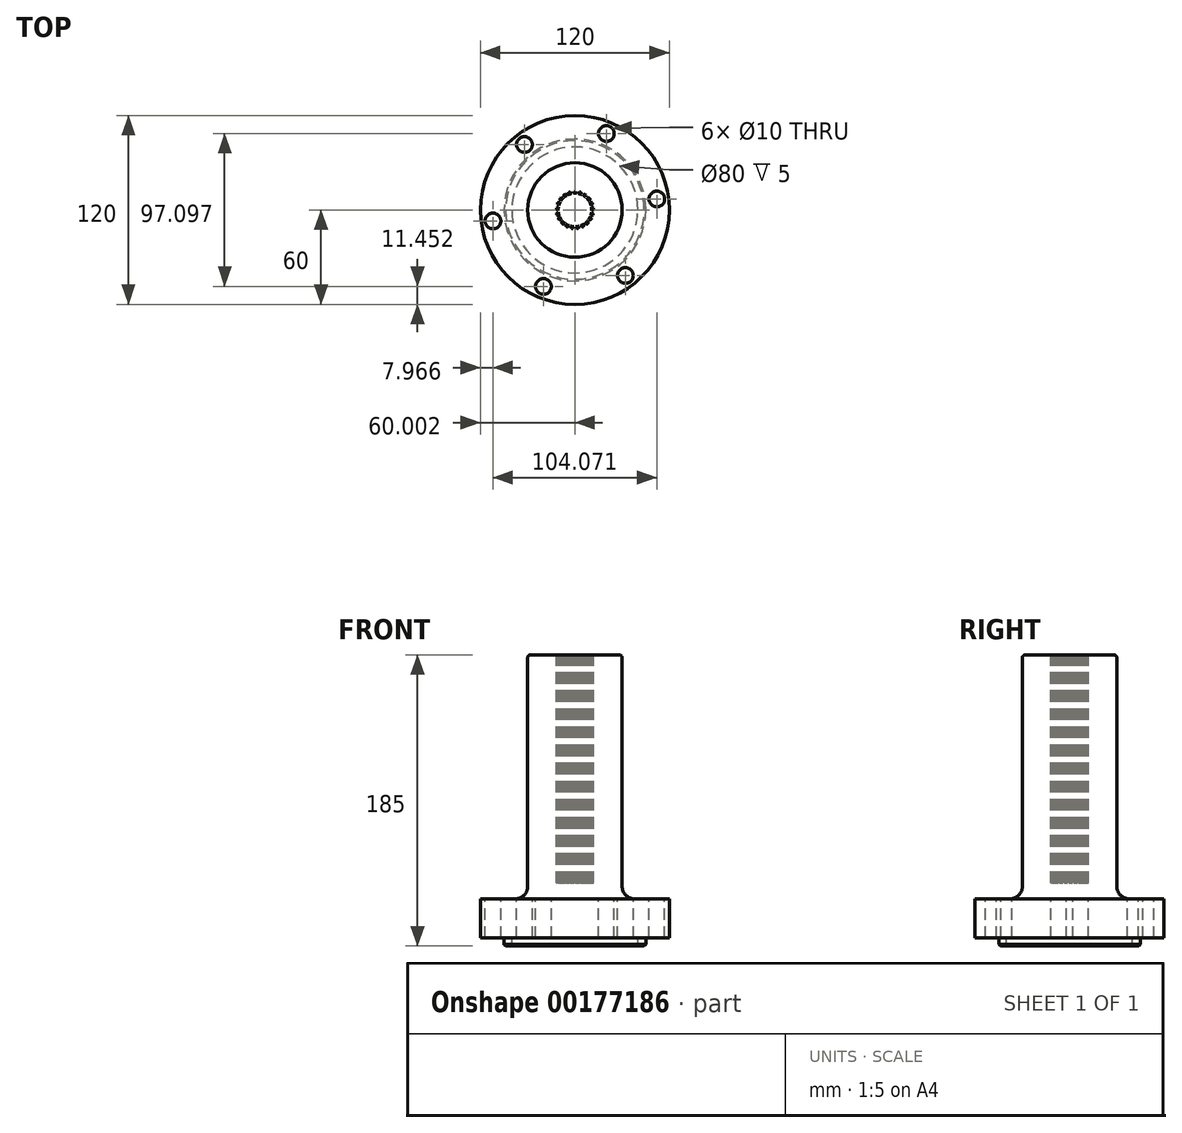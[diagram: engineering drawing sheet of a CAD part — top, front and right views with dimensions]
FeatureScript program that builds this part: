
annotation { "Feature Type Name" : "Feature", "Feature Type Description" : "" }
export const myFeature = defineFeature(function(context is Context, id is Id, definition is map)
    precondition{}
    {
        {
            var Q0;
            Q0=qCreatedBy(makeId("Front.planeOp"),FACE);
            var sketch = newSketch(context, id + "F0", { "sketchPlane" : qUnion([Q0])});
            skLineSegment(sketch, "E0", {"start": v(259.02, -43.78) * mm, "end": v(259.02, -223.78) * mm});
            skLineSegment(sketch, "E1", {"start": v(259.02, -223.78) * mm, "end": v(319.02, -223.78) * mm});
            skLineSegment(sketch, "E2", {"start": v(319.02, -223.78) * mm, "end": v(319.02, -198.78) * mm});
            skLineSegment(sketch, "E3", {"start": v(319.02, -198.78) * mm, "end": v(289.02, -198.78) * mm});
            skLineSegment(sketch, "E4", {"start": v(289.02, -198.78) * mm, "end": v(289.02, -43.78) * mm});
            skLineSegment(sketch, "E5", {"start": v(289.02, -43.78) * mm, "end": v(259.02, -43.78) * mm});
            skSolve(sketch);
        }
        {
            var Q0;
            Q0 = qSketchRegion(id + "F0", true);
            var Q1;
            Q1=sQuery(id+"F0.wireOp",EDGE,"E0");
            revolve(context, id + "F1", {"surfaceOperationType" : NewSurfaceOperationType.NEW, "entities" : qUnion([Q0]), "axis" : qUnion([Q1]), "revolveType" : RevolveType.FULL});
        }
        {
            var Q0;
            Q0=makeQuery(id+"F1.opRevolve","SWEPT_FACE",FACE,{"disambiguationData":[OSD([sQuery(id+"F0.wireOp",EDGE,"E5")])]});
            var sketch = newSketch(context, id + "F2", { "sketchPlane" : qUnion([Q0])});
            skCircle(sketch, "E6", {"center": v(259.02, 0) * mm, "radius": 11.83 * mm});
            skCircle(sketch, "E7", {"center": v(259.02, 0) * mm, "radius": 10.62 * mm});
            skLineSegment(sketch, "E8", {"start": v(258.54, -10.6) * mm, "end": v(257.73, -11.76) * mm});
            skLineSegment(sketch, "E9", {"start": v(259.5, -10.6) * mm, "end": v(260.3, -11.76) * mm});
            skLineSegment(sketch, "E10", {"start": v(258.54, -10.6) * mm, "end": v(259.5, -10.6) * mm});
            skLineSegment(sketch, "E11", {"start": v(257.73, -11.76) * mm, "end": v(260.3, -11.76) * mm});
            skPoint(sketch, "E12", {"position": v(259.02, -10.6) * mm});
            skPoint(sketch, "E13", {"position": v(259.02, -11.76) * mm});
            skLineSegment(sketch, "E14.1.0", {"start": v(261.7, -10.28) * mm, "end": v(262.6, -10) * mm});
            skLineSegment(sketch, "E14.1.1", {"start": v(262.6, -10) * mm, "end": v(263.72, -10.86) * mm});
            skLineSegment(sketch, "E14.1.2", {"start": v(261.7, -10.28) * mm, "end": v(261.26, -11.62) * mm});
            skLineSegment(sketch, "E14.1.3", {"start": v(261.26, -11.62) * mm, "end": v(263.72, -10.86) * mm});
            skLineSegment(sketch, "E14.2.0", {"start": v(264.6, -9.04) * mm, "end": v(265.4, -8.5) * mm});
            skLineSegment(sketch, "E14.2.1", {"start": v(265.4, -8.5) * mm, "end": v(266.7, -9) * mm});
            skLineSegment(sketch, "E14.2.2", {"start": v(264.6, -9.04) * mm, "end": v(264.58, -10.44) * mm});
            skLineSegment(sketch, "E14.2.3", {"start": v(264.58, -10.44) * mm, "end": v(266.7, -9) * mm});
            skLineSegment(sketch, "E14.3.0", {"start": v(267.02, -6.99) * mm, "end": v(267.62, -6.24) * mm});
            skLineSegment(sketch, "E14.3.1", {"start": v(267.62, -6.24) * mm, "end": v(269.02, -6.33) * mm});
            skLineSegment(sketch, "E14.3.2", {"start": v(267.02, -6.99) * mm, "end": v(267.41, -8.34) * mm});
            skLineSegment(sketch, "E14.3.3", {"start": v(267.41, -8.34) * mm, "end": v(269.02, -6.33) * mm});
            skLineSegment(sketch, "E14.4.0", {"start": v(268.72, -4.32) * mm, "end": v(269.07, -3.43) * mm});
            skLineSegment(sketch, "E14.4.1", {"start": v(269.07, -3.43) * mm, "end": v(270.44, -3.1) * mm});
            skLineSegment(sketch, "E14.4.2", {"start": v(268.72, -4.32) * mm, "end": v(269.5, -5.5) * mm});
            skLineSegment(sketch, "E14.4.3", {"start": v(269.5, -5.5) * mm, "end": v(270.44, -3.1) * mm});
            skLineSegment(sketch, "E14.5.0", {"start": v(269.57, -1.27) * mm, "end": v(269.64, -0.31) * mm});
            skLineSegment(sketch, "E14.5.1", {"start": v(269.64, -0.31) * mm, "end": v(270.85, 0.4) * mm});
            skLineSegment(sketch, "E14.5.2", {"start": v(269.57, -1.27) * mm, "end": v(270.65, -2.16) * mm});
            skLineSegment(sketch, "E14.5.3", {"start": v(270.65, -2.16) * mm, "end": v(270.85, 0.4) * mm});
            skLineSegment(sketch, "E14.6.0", {"start": v(269.47, 1.9) * mm, "end": v(269.26, 2.83) * mm});
            skLineSegment(sketch, "E14.6.1", {"start": v(269.26, 2.83) * mm, "end": v(270.2, 3.87) * mm});
            skLineSegment(sketch, "E14.6.2", {"start": v(269.47, 1.9) * mm, "end": v(270.77, 1.36) * mm});
            skLineSegment(sketch, "E14.6.3", {"start": v(270.77, 1.36) * mm, "end": v(270.2, 3.87) * mm});
            skLineSegment(sketch, "E14.7.0", {"start": v(268.45, 4.89) * mm, "end": v(267.97, 5.72) * mm});
            skLineSegment(sketch, "E14.7.1", {"start": v(267.97, 5.72) * mm, "end": v(268.56, 7) * mm});
            skLineSegment(sketch, "E14.7.2", {"start": v(268.45, 4.89) * mm, "end": v(269.85, 4.77) * mm});
            skLineSegment(sketch, "E14.7.3", {"start": v(269.85, 4.77) * mm, "end": v(268.56, 7) * mm});
            skLineSegment(sketch, "E14.8.0", {"start": v(266.59, 7.45) * mm, "end": v(265.89, 8.1) * mm});
            skLineSegment(sketch, "E14.8.1", {"start": v(265.89, 8.1) * mm, "end": v(266.08, 9.5) * mm});
            skLineSegment(sketch, "E14.8.2", {"start": v(266.59, 7.45) * mm, "end": v(267.96, 7.75) * mm});
            skLineSegment(sketch, "E14.8.3", {"start": v(267.96, 7.75) * mm, "end": v(266.08, 9.5) * mm});
            skLineSegment(sketch, "E14.9.0", {"start": v(264.06, 9.35) * mm, "end": v(263.2, 9.77) * mm});
            skLineSegment(sketch, "E14.9.1", {"start": v(263.2, 9.77) * mm, "end": v(262.96, 11.15) * mm});
            skLineSegment(sketch, "E14.9.2", {"start": v(264.06, 9.35) * mm, "end": v(265.28, 10.04) * mm});
            skLineSegment(sketch, "E14.9.3", {"start": v(265.28, 10.04) * mm, "end": v(262.96, 11.15) * mm});
            skLineSegment(sketch, "E14.10.0", {"start": v(261.08, 10.42) * mm, "end": v(260.13, 10.56) * mm});
            skLineSegment(sketch, "E14.10.1", {"start": v(260.13, 10.56) * mm, "end": v(259.5, 11.82) * mm});
            skLineSegment(sketch, "E14.10.2", {"start": v(261.08, 10.42) * mm, "end": v(262.05, 11.44) * mm});
            skLineSegment(sketch, "E14.10.3", {"start": v(262.05, 11.44) * mm, "end": v(259.5, 11.82) * mm});
            skLineSegment(sketch, "E14.11.0", {"start": v(257.92, 10.56) * mm, "end": v(256.97, 10.42) * mm});
            skLineSegment(sketch, "E14.11.1", {"start": v(256.97, 10.42) * mm, "end": v(256, 11.44) * mm});
            skLineSegment(sketch, "E14.11.2", {"start": v(257.92, 10.56) * mm, "end": v(258.54, 11.82) * mm});
            skLineSegment(sketch, "E14.11.3", {"start": v(258.54, 11.82) * mm, "end": v(256, 11.44) * mm});
            skLineSegment(sketch, "E14.12.0", {"start": v(254.85, 9.77) * mm, "end": v(253.99, 9.35) * mm});
            skLineSegment(sketch, "E14.12.1", {"start": v(253.99, 9.35) * mm, "end": v(252.76, 10.04) * mm});
            skLineSegment(sketch, "E14.12.2", {"start": v(254.85, 9.77) * mm, "end": v(255.08, 11.15) * mm});
            skLineSegment(sketch, "E14.12.3", {"start": v(255.08, 11.15) * mm, "end": v(252.76, 10.04) * mm});
            skLineSegment(sketch, "E14.13.0", {"start": v(252.16, 8.1) * mm, "end": v(251.45, 7.45) * mm});
            skLineSegment(sketch, "E14.13.1", {"start": v(251.45, 7.45) * mm, "end": v(250.08, 7.75) * mm});
            skLineSegment(sketch, "E14.13.2", {"start": v(252.16, 8.1) * mm, "end": v(251.97, 9.5) * mm});
            skLineSegment(sketch, "E14.13.3", {"start": v(251.97, 9.5) * mm, "end": v(250.08, 7.75) * mm});
            skLineSegment(sketch, "E14.14.0", {"start": v(250.07, 5.72) * mm, "end": v(249.6, 4.89) * mm});
            skLineSegment(sketch, "E14.14.1", {"start": v(249.6, 4.89) * mm, "end": v(248.2, 4.77) * mm});
            skLineSegment(sketch, "E14.14.2", {"start": v(250.07, 5.72) * mm, "end": v(249.48, 7) * mm});
            skLineSegment(sketch, "E14.14.3", {"start": v(249.48, 7) * mm, "end": v(248.2, 4.77) * mm});
            skLineSegment(sketch, "E14.15.0", {"start": v(248.79, 2.83) * mm, "end": v(248.57, 1.9) * mm});
            skLineSegment(sketch, "E14.15.1", {"start": v(248.57, 1.9) * mm, "end": v(247.27, 1.36) * mm});
            skLineSegment(sketch, "E14.15.2", {"start": v(248.79, 2.83) * mm, "end": v(247.84, 3.87) * mm});
            skLineSegment(sketch, "E14.15.3", {"start": v(247.84, 3.87) * mm, "end": v(247.27, 1.36) * mm});
            skLineSegment(sketch, "E14.16.0", {"start": v(248.4, -0.31) * mm, "end": v(248.48, -1.27) * mm});
            skLineSegment(sketch, "E14.16.1", {"start": v(248.48, -1.27) * mm, "end": v(247.4, -2.16) * mm});
            skLineSegment(sketch, "E14.16.2", {"start": v(248.4, -0.31) * mm, "end": v(247.2, 0.4) * mm});
            skLineSegment(sketch, "E14.16.3", {"start": v(247.2, 0.4) * mm, "end": v(247.4, -2.16) * mm});
            skLineSegment(sketch, "E14.17.0", {"start": v(248.97, -3.43) * mm, "end": v(249.32, -4.32) * mm});
            skLineSegment(sketch, "E14.17.1", {"start": v(249.32, -4.32) * mm, "end": v(248.55, -5.5) * mm});
            skLineSegment(sketch, "E14.17.2", {"start": v(248.97, -3.43) * mm, "end": v(247.6, -3.1) * mm});
            skLineSegment(sketch, "E14.17.3", {"start": v(247.6, -3.1) * mm, "end": v(248.55, -5.5) * mm});
            skLineSegment(sketch, "E14.18.0", {"start": v(250.43, -6.24) * mm, "end": v(251.03, -6.99) * mm});
            skLineSegment(sketch, "E14.18.1", {"start": v(251.03, -6.99) * mm, "end": v(250.63, -8.34) * mm});
            skLineSegment(sketch, "E14.18.2", {"start": v(250.43, -6.24) * mm, "end": v(249.03, -6.33) * mm});
            skLineSegment(sketch, "E14.18.3", {"start": v(249.03, -6.33) * mm, "end": v(250.63, -8.34) * mm});
            skLineSegment(sketch, "E14.19.0", {"start": v(252.65, -8.5) * mm, "end": v(253.44, -9.04) * mm});
            skLineSegment(sketch, "E14.19.1", {"start": v(253.44, -9.04) * mm, "end": v(253.46, -10.44) * mm});
            skLineSegment(sketch, "E14.19.2", {"start": v(252.65, -8.5) * mm, "end": v(251.33, -9) * mm});
            skLineSegment(sketch, "E14.19.3", {"start": v(251.33, -9) * mm, "end": v(253.46, -10.44) * mm});
            skLineSegment(sketch, "E14.20.0", {"start": v(255.44, -10) * mm, "end": v(256.35, -10.28) * mm});
            skLineSegment(sketch, "E14.20.1", {"start": v(256.35, -10.28) * mm, "end": v(256.79, -11.62) * mm});
            skLineSegment(sketch, "E14.20.2", {"start": v(255.44, -10) * mm, "end": v(254.33, -10.86) * mm});
            skLineSegment(sketch, "E14.20.3", {"start": v(254.33, -10.86) * mm, "end": v(256.79, -11.62) * mm});
            skSolve(sketch);
        }
        {
            var Q0;
            {var subQ0=sQuery(id+"F2.wireOp",EDGE,"E14.8.1");Q0=makeQuery(id+"F2.imprint","IMPRINT",FACE,{"disambiguationData":[TD([[makeQuery(id+"F2.imprint","IMPRINT",EDGE,{"derivedFrom":subQ0}),1.0]])]});}
            var Q1;
            {var subQ0=sQuery(id+"F2.wireOp",EDGE,"E10");Q1=makeQuery(id+"F2.imprint","IMPRINT",FACE,{"disambiguationData":[TD([[makeQuery(id+"F2.imprint","IMPRINT",EDGE,{"derivedFrom":subQ0}),1.0]])]});}
            var Q2;
            {var subQ0=sQuery(id+"F2.wireOp",EDGE,"E14.9.1");Q2=makeQuery(id+"F2.imprint","IMPRINT",FACE,{"disambiguationData":[TD([[makeQuery(id+"F2.imprint","IMPRINT",EDGE,{"derivedFrom":subQ0}),1.0]])]});}
            var Q3;
            {var subQ0=sQuery(id+"F2.wireOp",EDGE,"E14.10.1");Q3=makeQuery(id+"F2.imprint","IMPRINT",FACE,{"disambiguationData":[TD([[makeQuery(id+"F2.imprint","IMPRINT",EDGE,{"derivedFrom":subQ0}),1.0]])]});}
            var Q4;
            {var subQ0=sQuery(id+"F2.wireOp",EDGE,"E14.11.1");Q4=makeQuery(id+"F2.imprint","IMPRINT",FACE,{"disambiguationData":[TD([[makeQuery(id+"F2.imprint","IMPRINT",EDGE,{"derivedFrom":subQ0}),1.0]])]});}
            var Q5;
            {var subQ0=sQuery(id+"F2.wireOp",EDGE,"E14.12.1");Q5=makeQuery(id+"F2.imprint","IMPRINT",FACE,{"disambiguationData":[TD([[makeQuery(id+"F2.imprint","IMPRINT",EDGE,{"derivedFrom":subQ0}),1.0]])]});}
            var Q6;
            {var subQ0=sQuery(id+"F2.wireOp",EDGE,"E14.13.1");Q6=makeQuery(id+"F2.imprint","IMPRINT",FACE,{"disambiguationData":[TD([[makeQuery(id+"F2.imprint","IMPRINT",EDGE,{"derivedFrom":subQ0}),1.0]])]});}
            var Q7;
            {var subQ0=sQuery(id+"F2.wireOp",EDGE,"E14.14.1");Q7=makeQuery(id+"F2.imprint","IMPRINT",FACE,{"disambiguationData":[TD([[makeQuery(id+"F2.imprint","IMPRINT",EDGE,{"derivedFrom":subQ0}),1.0]])]});}
            var Q8;
            {var subQ0=sQuery(id+"F2.wireOp",EDGE,"E14.15.1");Q8=makeQuery(id+"F2.imprint","IMPRINT",FACE,{"disambiguationData":[TD([[makeQuery(id+"F2.imprint","IMPRINT",EDGE,{"derivedFrom":subQ0}),1.0]])]});}
            var Q9;
            {var subQ0=sQuery(id+"F2.wireOp",EDGE,"E14.16.1");Q9=makeQuery(id+"F2.imprint","IMPRINT",FACE,{"disambiguationData":[TD([[makeQuery(id+"F2.imprint","IMPRINT",EDGE,{"derivedFrom":subQ0}),1.0]])]});}
            var Q10;
            {var subQ0=sQuery(id+"F2.wireOp",EDGE,"E14.17.1");Q10=makeQuery(id+"F2.imprint","IMPRINT",FACE,{"disambiguationData":[TD([[makeQuery(id+"F2.imprint","IMPRINT",EDGE,{"derivedFrom":subQ0}),1.0]])]});}
            var Q11;
            {var subQ0=sQuery(id+"F2.wireOp",EDGE,"E14.18.1");Q11=makeQuery(id+"F2.imprint","IMPRINT",FACE,{"disambiguationData":[TD([[makeQuery(id+"F2.imprint","IMPRINT",EDGE,{"derivedFrom":subQ0}),1.0]])]});}
            var Q12;
            {var subQ0=sQuery(id+"F2.wireOp",EDGE,"E14.19.1");Q12=makeQuery(id+"F2.imprint","IMPRINT",FACE,{"disambiguationData":[TD([[makeQuery(id+"F2.imprint","IMPRINT",EDGE,{"derivedFrom":subQ0}),1.0]])]});}
            var Q13;
            {var subQ0=sQuery(id+"F2.wireOp",EDGE,"E8");Q13=makeQuery(id+"F2.imprint","IMPRINT",FACE,{"disambiguationData":[TD([[makeQuery(id+"F2.imprint","IMPRINT",EDGE,{"derivedFrom":subQ0}),-1.0]])]});}
            var Q14;
            {var subQ0=sQuery(id+"F2.wireOp",EDGE,"E9");Q14=makeQuery(id+"F2.imprint","IMPRINT",FACE,{"disambiguationData":[TD([[makeQuery(id+"F2.imprint","IMPRINT",EDGE,{"derivedFrom":subQ0}),1.0]])]});}
            var Q15;
            {var subQ0=sQuery(id+"F2.wireOp",EDGE,"E14.1.1");Q15=makeQuery(id+"F2.imprint","IMPRINT",FACE,{"disambiguationData":[TD([[makeQuery(id+"F2.imprint","IMPRINT",EDGE,{"derivedFrom":subQ0}),1.0]])]});}
            var Q16;
            {var subQ0=sQuery(id+"F2.wireOp",EDGE,"E14.2.1");Q16=makeQuery(id+"F2.imprint","IMPRINT",FACE,{"disambiguationData":[TD([[makeQuery(id+"F2.imprint","IMPRINT",EDGE,{"derivedFrom":subQ0}),1.0]])]});}
            var Q17;
            {var subQ0=sQuery(id+"F2.wireOp",EDGE,"E14.3.1");Q17=makeQuery(id+"F2.imprint","IMPRINT",FACE,{"disambiguationData":[TD([[makeQuery(id+"F2.imprint","IMPRINT",EDGE,{"derivedFrom":subQ0}),1.0]])]});}
            var Q18;
            {var subQ0=sQuery(id+"F2.wireOp",EDGE,"E14.4.1");Q18=makeQuery(id+"F2.imprint","IMPRINT",FACE,{"disambiguationData":[TD([[makeQuery(id+"F2.imprint","IMPRINT",EDGE,{"derivedFrom":subQ0}),1.0]])]});}
            var Q19;
            {var subQ0=sQuery(id+"F2.wireOp",EDGE,"E14.5.1");Q19=makeQuery(id+"F2.imprint","IMPRINT",FACE,{"disambiguationData":[TD([[makeQuery(id+"F2.imprint","IMPRINT",EDGE,{"derivedFrom":subQ0}),1.0]])]});}
            var Q20;
            {var subQ0=sQuery(id+"F2.wireOp",EDGE,"E14.6.1");Q20=makeQuery(id+"F2.imprint","IMPRINT",FACE,{"disambiguationData":[TD([[makeQuery(id+"F2.imprint","IMPRINT",EDGE,{"derivedFrom":subQ0}),1.0]])]});}
            var Q21;
            {var subQ0=sQuery(id+"F2.wireOp",EDGE,"E14.7.1");Q21=makeQuery(id+"F2.imprint","IMPRINT",FACE,{"disambiguationData":[TD([[makeQuery(id+"F2.imprint","IMPRINT",EDGE,{"derivedFrom":subQ0}),1.0]])]});}
            extrude(context, id + "F3", {"entities" : qUnion([Q0, Q1, Q2, Q3, Q4, Q5, Q6, Q7, Q8, Q9, Q10, Q11, Q12, Q13, Q14, Q15, Q16, Q17, Q18, Q19, Q20, Q21]), "operationType" : NewBodyOperationType.REMOVE, "oppositeDirection" : true, "depth" : 145 * mm, "offsetDistance" : 25 * mm});
        }
        {
            var Q0;
            Q0=makeQuery(id+"F1.opRevolve","SWEPT_FACE",FACE,{"disambiguationData":[OSD([sQuery(id+"F0.wireOp",EDGE,"E1")])]});
            var sketch = newSketch(context, id + "F4", { "sketchPlane" : qUnion([Q0])});
            skCircle(sketch, "E15", {"center": v(259.02, 0) * mm, "radius": 45 * mm});
            skCircle(sketch, "E16", {"center": v(259.02, 0) * mm, "radius": 40 * mm});
            skSolve(sketch);
        }
        {
            var Q0;
            Q0=makeQuery(id+"F4.imprint","IMPRINT",FACE,{"disambiguationData":[TD([[makeQuery(id+"F4.imprint","IMPRINT",EDGE,{"derivedFrom":sQuery(id+"F4.wireOp",EDGE,"E15")}),1.0]])]});
            extrude(context, id + "F5", {"entities" : qUnion([Q0]), "operationType" : NewBodyOperationType.ADD, "depth" : 5 * mm, "offsetDistance" : 25 * mm});
        }
        {
            var Q0;
            Q0=makeQuery(id+"F1.opRevolve","SWEPT_FACE",FACE,{"disambiguationData":[OSD([sQuery(id+"F0.wireOp",EDGE,"E3")])]});
            var sketch = newSketch(context, id + "F6", { "sketchPlane" : qUnion([Q0])});
            skCircle(sketch, "E17", {"center": v(206.99, -6.97) * mm, "radius": 5 * mm});
            skCircle(sketch, "E18.1.0", {"center": v(239.04, -48.55) * mm, "radius": 5 * mm});
            skCircle(sketch, "E18.2.0", {"center": v(291.07, -41.58) * mm, "radius": 5 * mm});
            skCircle(sketch, "E18.3.0", {"center": v(311.06, 6.97) * mm, "radius": 5 * mm});
            skCircle(sketch, "E18.4.0", {"center": v(279, 48.55) * mm, "radius": 5 * mm});
            skCircle(sketch, "E18.5.0", {"center": v(226.97, 41.58) * mm, "radius": 5 * mm});
            skPoint(sketch, "E18.center", {"position": v(259.02, 0) * mm});
            skSolve(sketch);
        }
        {
            var Q0;
            Q0=makeQuery(id+"F6.imprint","IMPRINT",FACE,{"disambiguationData":[TD([[makeQuery(id+"F6.imprint","IMPRINT",EDGE,{"derivedFrom":sQuery(id+"F6.wireOp",EDGE,"E17")}),1.0]])]});
            var Q1;
            Q1=makeQuery(id+"F6.imprint","IMPRINT",FACE,{"disambiguationData":[TD([[makeQuery(id+"F6.imprint","IMPRINT",EDGE,{"derivedFrom":sQuery(id+"F6.wireOp",EDGE,"E18.5.0")}),1.0]])]});
            var Q2;
            Q2=makeQuery(id+"F6.imprint","IMPRINT",FACE,{"disambiguationData":[TD([[makeQuery(id+"F6.imprint","IMPRINT",EDGE,{"derivedFrom":sQuery(id+"F6.wireOp",EDGE,"E18.3.0")}),1.0]])]});
            var Q3;
            Q3=makeQuery(id+"F6.imprint","IMPRINT",FACE,{"disambiguationData":[TD([[makeQuery(id+"F6.imprint","IMPRINT",EDGE,{"derivedFrom":sQuery(id+"F6.wireOp",EDGE,"E18.2.0")}),1.0]])]});
            var Q4;
            Q4=makeQuery(id+"F6.imprint","IMPRINT",FACE,{"disambiguationData":[TD([[makeQuery(id+"F6.imprint","IMPRINT",EDGE,{"derivedFrom":sQuery(id+"F6.wireOp",EDGE,"E18.1.0")}),1.0]])]});
            var Q5;
            Q5=makeQuery(id+"F6.imprint","IMPRINT",FACE,{"disambiguationData":[TD([[makeQuery(id+"F6.imprint","IMPRINT",EDGE,{"derivedFrom":sQuery(id+"F6.wireOp",EDGE,"E18.4.0")}),1.0]])]});
            var Q6;
            Q6=sQuery(id+"F6.wireOp",EDGE,"E17");
            var Q7;
            Q7=sQuery(id+"F6.wireOp",EDGE,"E18.5.0");
            var Q8;
            Q8=sQuery(id+"F6.wireOp",EDGE,"E18.4.0");
            var Q9;
            Q9=sQuery(id+"F6.wireOp",EDGE,"E18.3.0");
            var Q10;
            Q10=sQuery(id+"F6.wireOp",EDGE,"E18.2.0");
            var Q11;
            Q11=sQuery(id+"F6.wireOp",EDGE,"E18.1.0");
            extrude(context, id + "F7", {"entities" : qUnion([Q0, Q1, Q2, Q3, Q4, Q5]), "operationType" : NewBodyOperationType.REMOVE, "surfaceEntities" : qUnion([Q6, Q7, Q8, Q9, Q10, Q11]), "oppositeDirection" : true, "depth" : 63.7 * mm, "offsetDistance" : 25 * mm});
        }
        {
            var Q0;
            Q0=makeQuery(id+"F1.opRevolve","SWEPT_EDGE",EDGE,{"disambiguationData":[OSD([sQuery(id+"F0.wireOp",EDGE,"E3"),sQuery(id+"F0.wireOp",EDGE,"E4")])]});
            fillet(context, id + "F8", {"entities" : qUnion([Q0]), "radius" : 7.73 * mm, "tangentPropagation" : true, "allowEdgeOverflow" : false});
        }
        {
            var Q0;
            Q0=makeQuery(id+"Ft2N80KFrBvMJeg_1.boolean.opBoolean","COPY",EDGE,{"derivedFrom":makeQuery(id+"Ft2N80KFrBvMJeg_1.opExtrude","CAP_EDGE",EDGE,{"disambiguationData":[OSD([sQuery(id+"F2.wireOp",EDGE,"y8v2WqfD-jJEz-qQTw-g6It-ZQySjAIkKfFT")])],"isStart":true})});
            var Q1;
            Q1=makeQuery(id+"F1.opRevolve","SWEPT_EDGE",EDGE,{"disambiguationData":[OSD([sQuery(id+"F0.wireOp",EDGE,"E4"),sQuery(id+"F0.wireOp",EDGE,"E5")])]});
            fillet(context, id + "F9", {"entities" : qUnion([Q0, Q1]), "radius" : 2 * mm, "tangentPropagation" : true, "allowEdgeOverflow" : false});
        }
        {
            var Q0;
            Q0=makeQuery(id+"F5.opExtrude","CAP_EDGE",EDGE,{"disambiguationData":[OSD([sQuery(id+"F4.wireOp",EDGE,"E15")])],"isStart":false});
            chamfer(context, id + "F10", {"entities" : qUnion([Q0]), "width" : 1 * mm, "tangentPropagation" : true});
        }
    });
